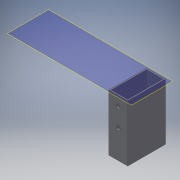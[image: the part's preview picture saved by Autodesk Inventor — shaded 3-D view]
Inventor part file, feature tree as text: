
AUTODESK INVENTOR PART (.ipt)
format: ipt  version: 2018 (Build 220112000, 112)  size: 120,832 bytes
history: native  units: in
note: dims shown in document units (in); Inventor stores cm internally (conversion verified against a paired STEP export)
features: extrude x2, sketch x2, other x2, plane x1
ambient origin geometry x8: Origin, YZ Plane, XZ Plane, XY Plane, X Axis, Y Axis, Z Axis, Center Point
bodies: Solid1 (feature_tree)
feature tree (7):
  plane  "Work Plane1"
  extrude  "Extrusion1"  Depth=2.0in
  extrude  "Extrusion2"  Depth=0.065in
  sketch  "Sketch1"  dims[d0=1.0in d1=2.0in]
  sketch  "Sketch2"  dims[d3=0.065in d4=0.065in d5=0.065in d6=0.065in d7=3.0in d8=0.0in d9=0.5in d10=1.0in d11=0.2031in d12=0.2031in d13=0.5in d14=0.5in d15=3.0in d16=0.0in]
  other  "non integrated hatch.iam"
  other  "left arm:1"
